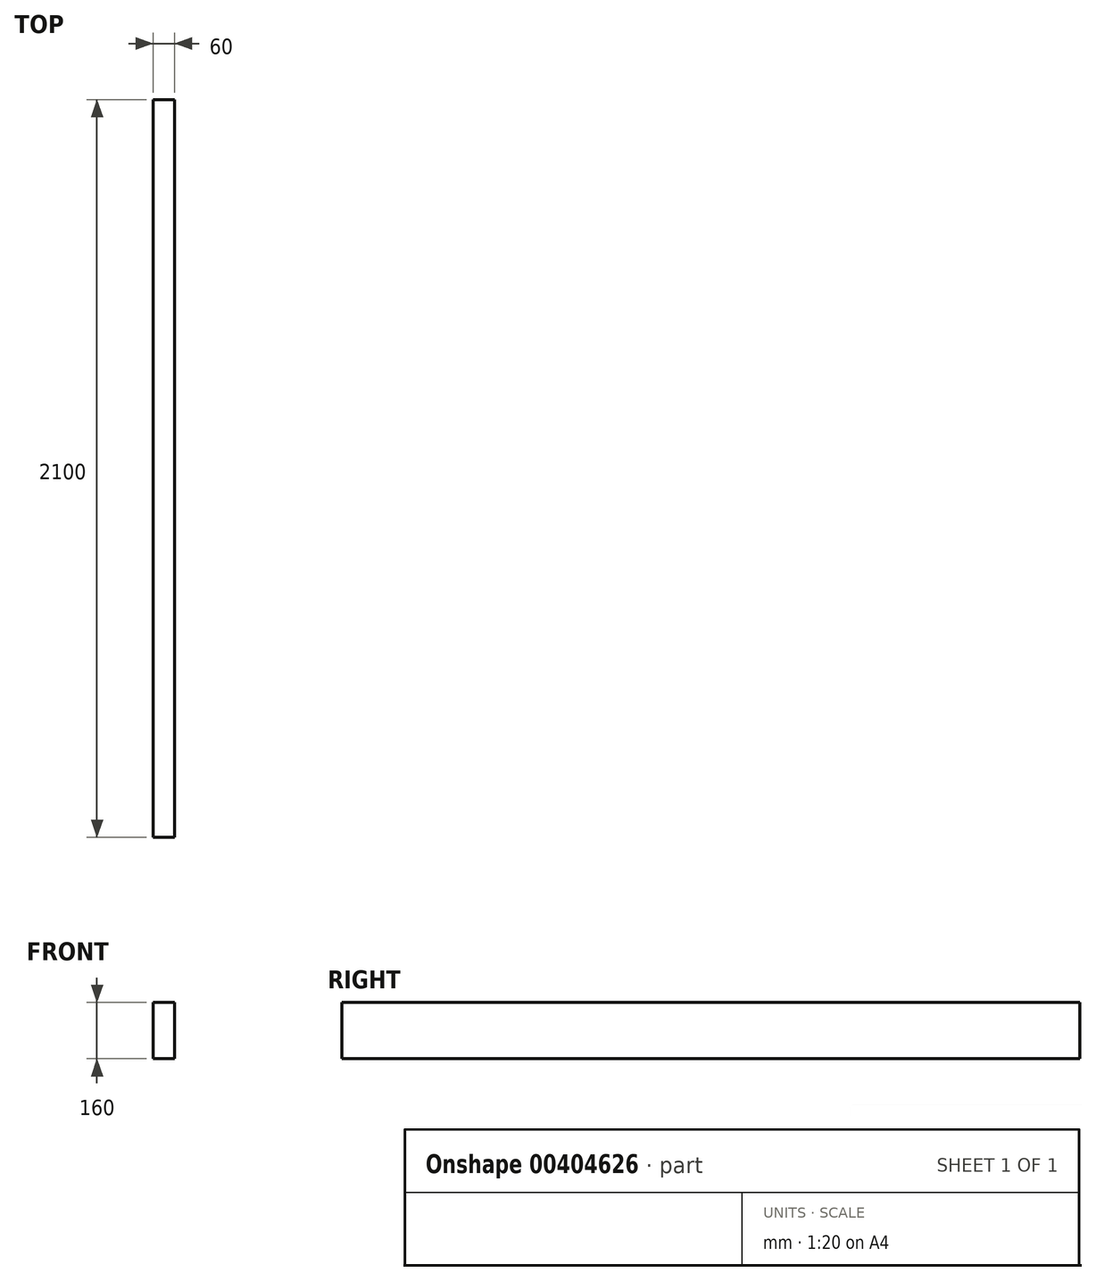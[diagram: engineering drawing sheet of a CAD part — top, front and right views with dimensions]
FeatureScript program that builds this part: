
annotation { "Feature Type Name" : "Feature", "Feature Type Description" : "" }
export const myFeature = defineFeature(function(context is Context, id is Id, definition is map)
    precondition{}
    {
        {
            var Q0;
            Q0=qCreatedBy(makeId("Front.planeOp"),FACE);
            var sketch = newSketch(context, id + "F0", { "sketchPlane" : qUnion([Q0])});
            skLineSegment(sketch, "E0.bottom", {"start": v(-30, 80) * mm, "end": v(30, 80) * mm});
            skLineSegment(sketch, "E0.top", {"start": v(-30, -80) * mm, "end": v(30, -80) * mm});
            skLineSegment(sketch, "E0.left", {"start": v(-30, 80) * mm, "end": v(-30, -80) * mm});
            skLineSegment(sketch, "E0.right", {"start": v(30, 80) * mm, "end": v(30, -80) * mm});
            skSolve(sketch);
        }
        {
            var Q0;
            Q0=qSketchRegion(id+"F0",true);
            extrude(context, id + "F1", {"entities" : qUnion([Q0]), "depth" : 2100 * mm});
        }
    });
